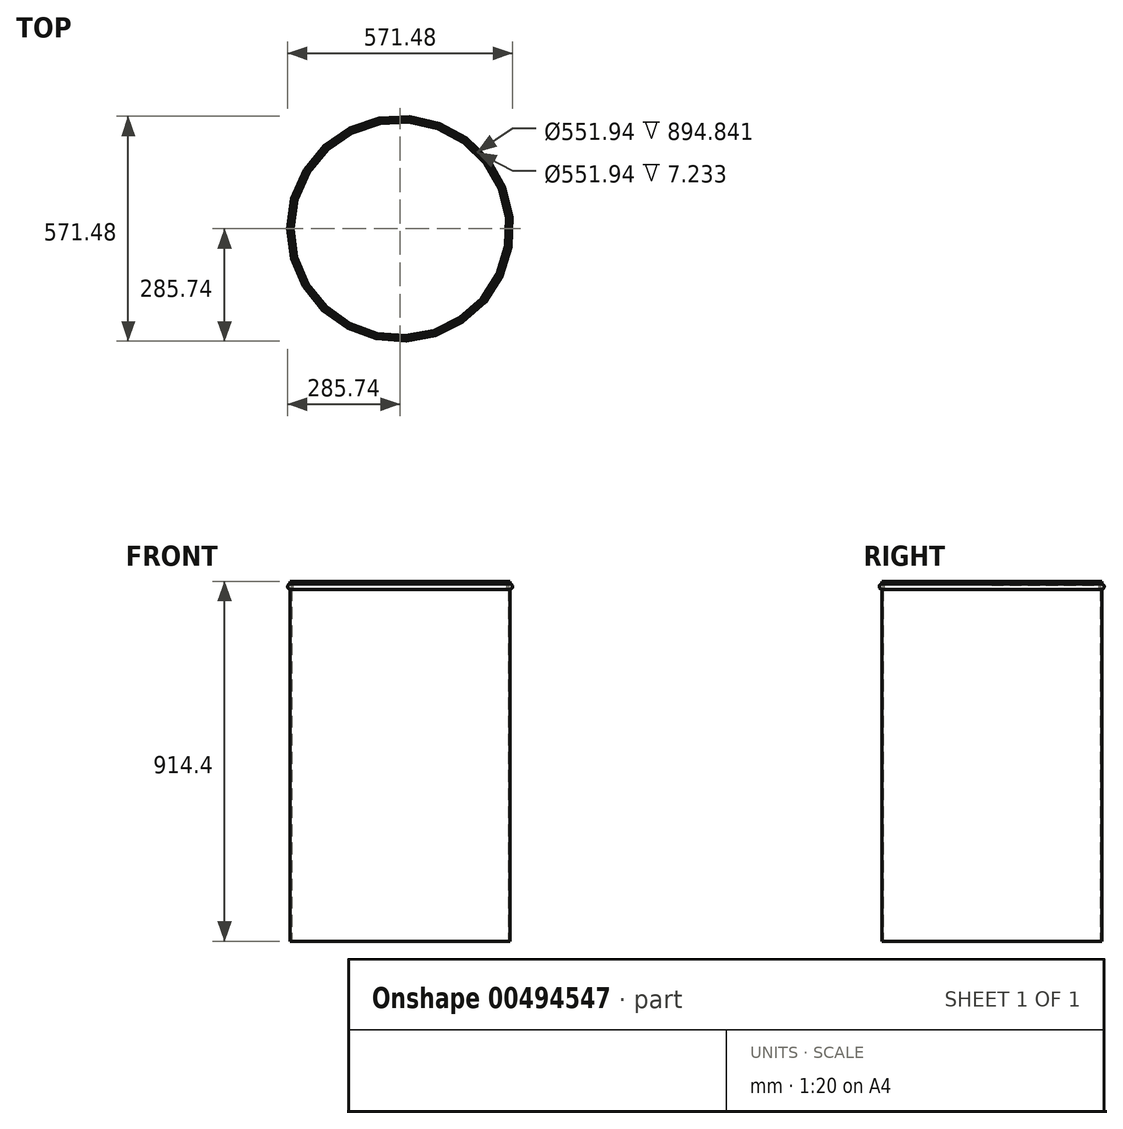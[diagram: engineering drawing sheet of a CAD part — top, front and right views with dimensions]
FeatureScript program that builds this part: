
annotation { "Feature Type Name" : "Feature", "Feature Type Description" : "" }
export const myFeature = defineFeature(function(context is Context, id is Id, definition is map)
    precondition{}
    {
        {
            var Q0;
            Q0=qCreatedBy(makeId("Top.planeOp"),FACE);
            var sketch = newSketch(context, id + "F0", { "sketchPlane" : qUnion([Q0])});
            skCircle(sketch, "E0", {"center": v(0, 0) * mm, "radius": 279.4 * mm});
            skCircle(sketch, "E1", {"center": v(0, 0) * mm, "radius": 275.97 * mm});
            skSolve(sketch);
        }
        {
            var Q0;
            Q0=qSketchRegion(id+"F0",true);
            extrude(context, id + "F1", {"entities" : qUnion([Q0]), "depth" : 914.4 * mm});
        }
        {
            var Q0;
            Q0=qCreatedBy(makeId("Front.planeOp"),FACE);
            var sketch = newSketch(context, id + "F2", { "sketchPlane" : qUnion([Q0])});
            skCircle(sketch, "E2", {"center": v(278.91, 901) * mm, "radius": 6.83 * mm});
            skSolve(sketch);
        }
        {
            var Q0;
            Q0=makeQuery(id+"F2.imprint","IMPRINT",FACE,{"disambiguationData":[TD([[makeQuery(id+"F2.imprint","IMPRINT",EDGE,{"derivedFrom":sQuery(id+"F2.wireOp",EDGE,"E2")}),1.0]])]});
            var Q1;
            Q1=sQuery(id+"F2.wireOp",EDGE,"E2");
            var Q2;
            Q2=makeQuery(id+"F1.opExtrude","CAP_EDGE",EDGE,{"disambiguationData":[OSD([sQuery(id+"F0.wireOp",EDGE,"E0")])],"isStart":false});
            revolve(context, id + "F3", {"operationType" : NewBodyOperationType.ADD, "entities" : qUnion([Q0]), "surfaceEntities" : qUnion([Q1]), "axis" : qUnion([Q2]), "revolveType" : RevolveType.FULL});
        }
        {
            var Q0;
            Q0=qCreatedBy(makeId("Front.planeOp"),FACE);
            var sketch = newSketch(context, id + "F4", { "sketchPlane" : qUnion([Q0])});
            skCircle(sketch, "E3", {"center": v(279.4, 900.93) * mm, "radius": 4.15 * mm});
            skSolve(sketch);
        }
        {
            var Q0;
            Q0 = qSketchRegion(id + "F4", true);
            var Q1;
            Q1=makeQuery(id+"F1.opExtrude","CAP_EDGE",EDGE,{"disambiguationData":[OSD([sQuery(id+"F0.wireOp",EDGE,"E0")])],"isStart":false});
            revolve(context, id + "F5", {"operationType" : NewBodyOperationType.REMOVE, "entities" : qUnion([Q0]), "axis" : qUnion([Q1]), "revolveType" : RevolveType.FULL, "oppositeDirection" : true});
        }
    });
